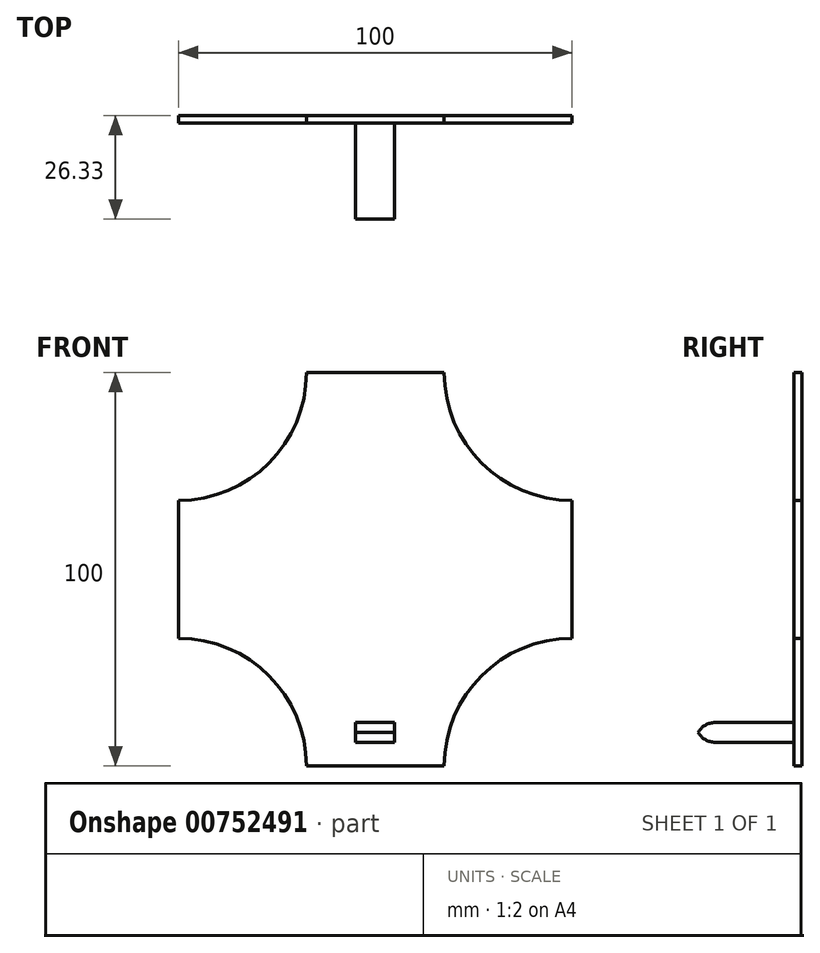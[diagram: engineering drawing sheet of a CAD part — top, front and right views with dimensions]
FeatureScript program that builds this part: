
annotation { "Feature Type Name" : "Feature", "Feature Type Description" : "" }
export const myFeature = defineFeature(function(context is Context, id is Id, definition is map)
    precondition{}
    {
        {
            var Q0;
            Q0=qCreatedBy(makeId("Front.planeOp"),FACE);
            var sketch = newSketch(context, id + "F0", { "sketchPlane" : qUnion([Q0])});
            skLineSegment(sketch, "E0.bottom", {"start": v(-72.44, 53.97) * mm, "end": v(27.56, 53.97) * mm});
            skLineSegment(sketch, "E0.top", {"start": v(-72.44, -46.03) * mm, "end": v(27.56, -46.03) * mm});
            skLineSegment(sketch, "E0.left", {"start": v(-72.44, 53.97) * mm, "end": v(-72.44, -46.03) * mm});
            skLineSegment(sketch, "E0.right", {"start": v(27.56, 53.97) * mm, "end": v(27.56, -46.03) * mm});
            skSolve(sketch);
        }
        {
            var Q0;
            Q0=makeQuery(id+"F0.imprint","IMPRINT",FACE,{"disambiguationData":[TD([[makeQuery(id+"F0.imprint","IMPRINT",EDGE,{"derivedFrom":sQuery(id+"F0.wireOp",EDGE,"E0.bottom")}),-1.0]])]});
            extrude(context, id + "F1", {"entities" : qUnion([Q0]), "depth" : 2 * mm, "offsetDistance" : 25 * mm});
        }
        {
            var Q0;
            Q0=makeQuery(id+"F1.opExtrude","CAP_FACE",FACE,{"disambiguationData":[OSD([sQuery(id+"F0.wireOp",EDGE,"E0.bottom"),sQuery(id+"F0.wireOp",EDGE,"E0.top"),sQuery(id+"F0.wireOp",EDGE,"E0.left"),sQuery(id+"F0.wireOp",EDGE,"E0.right")])],"isStart":false});
            var sketch = newSketch(context, id + "F2", { "sketchPlane" : qUnion([Q0])});
            skCircle(sketch, "E1", {"center": v(27.56, -46.03) * mm, "radius": 32.5 * mm});
            skCircle(sketch, "E2", {"center": v(-72.44, 53.97) * mm, "radius": 32.5 * mm});
            skCircle(sketch, "E3", {"center": v(27.56, 53.97) * mm, "radius": 32.5 * mm});
            skCircle(sketch, "E4", {"center": v(-72.44, -46.03) * mm, "radius": 32.5 * mm});
            skSolve(sketch);
        }
        {
            var Q0;
            {var subQ0=sQuery(id+"F2.wireOp",EDGE,"E4");var subQ1=makeQuery(id+"F1.opExtrude","CAP_EDGE",EDGE,{"disambiguationData":[OSD([sQuery(id+"F0.wireOp",EDGE,"E0.top")])],"isStart":false});var subQ2=makeQuery(id+"F2.imprint","INTERSECT",VERTEX,{"derivedFrom":[subQ1,subQ0]});Q0=makeQuery(id+"F2.imprint","IMPRINT",FACE,{"disambiguationData":[TD([[makeQuery(id+"F2.imprint","IMPRINT",EDGE,{"disambiguationData":[TD([[subQ2,1.0]])],"derivedFrom":subQ0}),1.0]])]});}
            var Q1;
            {var subQ0=sQuery(id+"F2.wireOp",EDGE,"E2");var subQ1=makeQuery(id+"F1.opExtrude","CAP_EDGE",EDGE,{"disambiguationData":[OSD([sQuery(id+"F0.wireOp",EDGE,"E0.bottom")])],"isStart":false});var subQ2=makeQuery(id+"F2.imprint","INTERSECT",VERTEX,{"derivedFrom":[subQ1,subQ0]});Q1=makeQuery(id+"F2.imprint","IMPRINT",FACE,{"disambiguationData":[TD([[makeQuery(id+"F2.imprint","IMPRINT",EDGE,{"disambiguationData":[TD([[subQ2,-1.0]])],"derivedFrom":subQ0}),1.0]])]});}
            var Q2;
            {var subQ0=sQuery(id+"F2.wireOp",EDGE,"E2");var subQ1=makeQuery(id+"F1.opExtrude","CAP_EDGE",EDGE,{"disambiguationData":[OSD([sQuery(id+"F0.wireOp",EDGE,"E0.bottom")])],"isStart":false});var subQ2=makeQuery(id+"F2.imprint","INTERSECT",VERTEX,{"derivedFrom":[subQ1,subQ0]});Q2=makeQuery(id+"F2.imprint","IMPRINT",FACE,{"disambiguationData":[TD([[makeQuery(id+"F2.imprint","IMPRINT",EDGE,{"disambiguationData":[TD([[subQ2,1.0]])],"derivedFrom":subQ0}),1.0]])]});}
            var Q3;
            {var subQ0=sQuery(id+"F2.wireOp",EDGE,"E3");var subQ1=makeQuery(id+"F1.opExtrude","CAP_EDGE",EDGE,{"disambiguationData":[OSD([sQuery(id+"F0.wireOp",EDGE,"E0.bottom")])],"isStart":false});var subQ2=makeQuery(id+"F2.imprint","INTERSECT",VERTEX,{"derivedFrom":[subQ1,subQ0]});Q3=makeQuery(id+"F2.imprint","IMPRINT",FACE,{"disambiguationData":[TD([[makeQuery(id+"F2.imprint","IMPRINT",EDGE,{"disambiguationData":[TD([[subQ2,1.0]])],"derivedFrom":subQ0}),1.0]])]});}
            var Q4;
            {var subQ0=sQuery(id+"F2.wireOp",EDGE,"E3");var subQ1=makeQuery(id+"F1.opExtrude","CAP_EDGE",EDGE,{"disambiguationData":[OSD([sQuery(id+"F0.wireOp",EDGE,"E0.bottom")])],"isStart":false});var subQ2=makeQuery(id+"F2.imprint","INTERSECT",VERTEX,{"derivedFrom":[subQ1,subQ0]});Q4=makeQuery(id+"F2.imprint","IMPRINT",FACE,{"disambiguationData":[TD([[makeQuery(id+"F2.imprint","IMPRINT",EDGE,{"disambiguationData":[TD([[subQ2,-1.0]])],"derivedFrom":subQ0}),1.0]])]});}
            var Q5;
            {var subQ0=sQuery(id+"F2.wireOp",EDGE,"E1");var subQ1=makeQuery(id+"F1.opExtrude","CAP_EDGE",EDGE,{"disambiguationData":[OSD([sQuery(id+"F0.wireOp",EDGE,"E0.top")])],"isStart":false});var subQ2=makeQuery(id+"F2.imprint","INTERSECT",VERTEX,{"derivedFrom":[subQ1,subQ0]});Q5=makeQuery(id+"F2.imprint","IMPRINT",FACE,{"disambiguationData":[TD([[makeQuery(id+"F2.imprint","IMPRINT",EDGE,{"disambiguationData":[TD([[subQ2,-1.0]])],"derivedFrom":subQ0}),1.0]])]});}
            var Q6;
            {var subQ0=sQuery(id+"F2.wireOp",EDGE,"E1");var subQ1=makeQuery(id+"F1.opExtrude","CAP_EDGE",EDGE,{"disambiguationData":[OSD([sQuery(id+"F0.wireOp",EDGE,"E0.top")])],"isStart":false});var subQ2=makeQuery(id+"F2.imprint","INTERSECT",VERTEX,{"derivedFrom":[subQ1,subQ0]});Q6=makeQuery(id+"F2.imprint","IMPRINT",FACE,{"disambiguationData":[TD([[makeQuery(id+"F2.imprint","IMPRINT",EDGE,{"disambiguationData":[TD([[subQ2,1.0]])],"derivedFrom":subQ0}),1.0]])]});}
            extrude(context, id + "F3", {"entities" : qUnion([Q0, Q1, Q2, Q3, Q4, Q5, Q6]), "operationType" : NewBodyOperationType.REMOVE, "oppositeDirection" : true, "depth" : 25 * mm, "offsetDistance" : 25 * mm});
        }
        {
            var Q0;
            Q0=makeQuery(id+"F1.opExtrude","CAP_FACE",FACE,{"disambiguationData":[OSD([sQuery(id+"F0.wireOp",EDGE,"E0.bottom"),sQuery(id+"F0.wireOp",EDGE,"E0.top"),sQuery(id+"F0.wireOp",EDGE,"E0.left"),sQuery(id+"F0.wireOp",EDGE,"E0.right")])],"isStart":false});
            var sketch = newSketch(context, id + "F4", { "sketchPlane" : qUnion([Q0])});
            skCircle(sketch, "E5", {"center": v(-72.44, -46.03) * mm, "radius": 32.5 * mm});
            skSolve(sketch);
        }
        {
            var Q0;
            {var subQ0=sQuery(id+"F4.wireOp",EDGE,"E5");var subQ1=makeQuery(id+"F1.opExtrude","CAP_EDGE",EDGE,{"disambiguationData":[OSD([sQuery(id+"F0.wireOp",EDGE,"E0.top")])],"isStart":false});var subQ2=makeQuery(id+"F4.imprint","INTERSECT",VERTEX,{"derivedFrom":[subQ1,subQ0]});Q0=makeQuery(id+"F4.imprint","IMPRINT",FACE,{"disambiguationData":[TD([[makeQuery(id+"F4.imprint","IMPRINT",EDGE,{"disambiguationData":[TD([[subQ2,1.0]])],"derivedFrom":subQ0}),1.0]])]});}
            var Q1;
            {var subQ0=sQuery(id+"F4.wireOp",EDGE,"E5");var subQ1=makeQuery(id+"F1.opExtrude","CAP_EDGE",EDGE,{"disambiguationData":[OSD([sQuery(id+"F0.wireOp",EDGE,"E0.top")])],"isStart":false});var subQ2=makeQuery(id+"F4.imprint","INTERSECT",VERTEX,{"derivedFrom":[subQ1,subQ0]});Q1=makeQuery(id+"F4.imprint","IMPRINT",FACE,{"disambiguationData":[TD([[makeQuery(id+"F4.imprint","IMPRINT",EDGE,{"disambiguationData":[TD([[subQ2,-1.0]])],"derivedFrom":subQ0}),1.0]])]});}
            extrude(context, id + "F5", {"entities" : qUnion([Q0, Q1]), "operationType" : NewBodyOperationType.REMOVE, "oppositeDirection" : true, "depth" : 25 * mm, "offsetDistance" : 25 * mm});
        }
        {
            var Q0;
            Q0=makeQuery(id+"F1.opExtrude","CAP_FACE",FACE,{"disambiguationData":[OSD([sQuery(id+"F0.wireOp",EDGE,"E0.bottom"),sQuery(id+"F0.wireOp",EDGE,"E0.top"),sQuery(id+"F0.wireOp",EDGE,"E0.left"),sQuery(id+"F0.wireOp",EDGE,"E0.right")])],"isStart":false});
            var sketch = newSketch(context, id + "F6", { "sketchPlane" : qUnion([Q0])});
            skLineSegment(sketch, "E6.bottom", {"start": v(-27.52, -34.96) * mm, "end": v(-17.52, -34.96) * mm});
            skLineSegment(sketch, "E6.top", {"start": v(-27.52, -39.96) * mm, "end": v(-17.52, -39.96) * mm});
            skLineSegment(sketch, "E6.left", {"start": v(-27.52, -34.96) * mm, "end": v(-27.52, -39.96) * mm});
            skLineSegment(sketch, "E6.right", {"start": v(-17.52, -34.96) * mm, "end": v(-17.52, -39.96) * mm});
            skSolve(sketch);
        }
        {
            var Q0;
            Q0=makeQuery(id+"F6.imprint","IMPRINT",FACE,{"disambiguationData":[TD([[makeQuery(id+"F6.imprint","IMPRINT",EDGE,{"derivedFrom":sQuery(id+"F6.wireOp",EDGE,"E6.bottom")}),-1.0]])]});
            extrude(context, id + "F7", {"entities" : qUnion([Q0]), "operationType" : NewBodyOperationType.ADD, "depth" : 25 * mm, "offsetDistance" : 25 * mm});
        }
        {
            var Q0;
            Q0=makeQuery(id+"F7.opExtrude","CAP_EDGE",EDGE,{"disambiguationData":[OSD([sQuery(id+"F6.wireOp",EDGE,"E6.bottom")])],"isStart":false});
            var Q1;
            Q1=makeQuery(id+"F7.opExtrude","CAP_EDGE",EDGE,{"disambiguationData":[OSD([sQuery(id+"F6.wireOp",EDGE,"E6.top")])],"isStart":false});
            fillet(context, id + "F8", {"entities" : qUnion([Q0, Q1]), "radius" : 5 * mm, "tangentPropagation" : true, "allowEdgeOverflow" : false});
        }
    });
